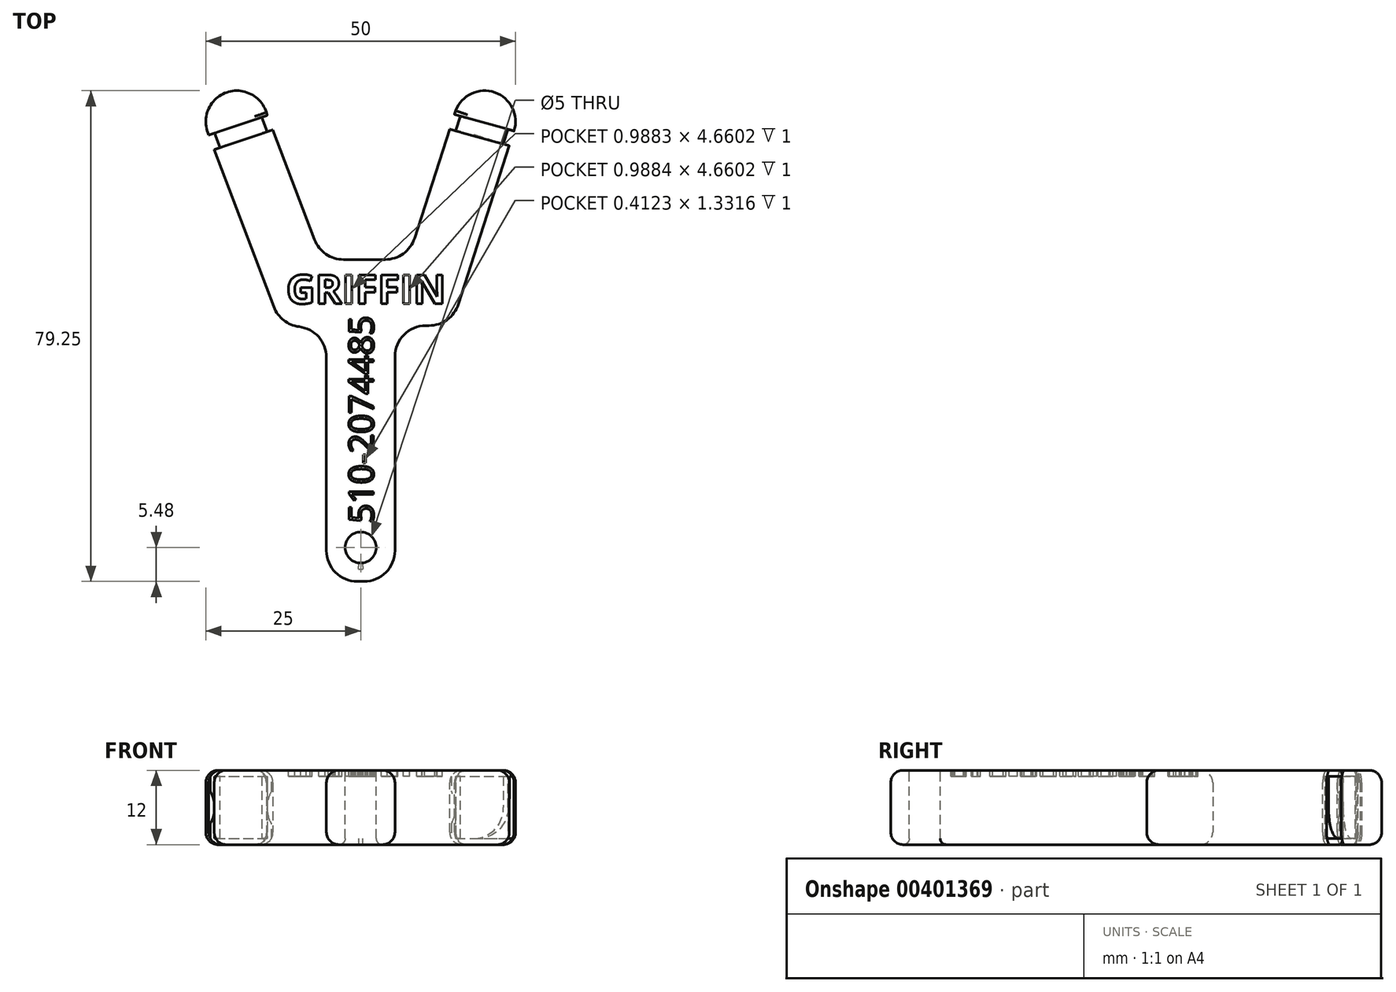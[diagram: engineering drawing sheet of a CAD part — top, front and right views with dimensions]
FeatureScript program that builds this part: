
annotation { "Feature Type Name" : "Feature", "Feature Type Description" : "" }
export const myFeature = defineFeature(function(context is Context, id is Id, definition is map)
    precondition{}
    {
        {
            var Q0;
            Q0=qCreatedBy(makeId("Top.planeOp"),FACE);
            var sketch = newSketch(context, id + "F0", { "sketchPlane" : qUnion([Q0])});
            skCircle(sketch, "E0", {"center": v(-20, 22.27) * mm, "radius": 1.5 * mm, "construction": true});
            skCircle(sketch, "E1", {"center": v(20, 22.27) * mm, "radius": 1.5 * mm, "construction": true});
            skArc(sketch, "E2", {"start": v(-15.23, 23.77) * mm, "mid": v(-21.63, 27) * mm, "end": v(-24.68, 20.5) * mm});
            skArc(sketch, "E3", {"start": v(24.76, 20.74) * mm, "mid": v(21.65, 27) * mm, "end": v(15.33, 24.05) * mm});
            skLineSegment(sketch, "E4", {"start": v(-15.44, 24.32) * mm, "end": v(-7.44, 3.23) * mm});
            skLineSegment(sketch, "E5", {"start": v(15.33, 24.05) * mm, "end": v(8.7, 3.47) * mm});
            skLineSegment(sketch, "E6", {"start": v(3.94, 0) * mm, "end": v(-2.77, 0) * mm});
            skLineSegment(sketch, "E7", {"start": v(-24.68, 20.5) * mm, "end": v(-12.8, -10.8) * mm});
            skLineSegment(sketch, "E8", {"start": v(-12.8, -10.8) * mm, "end": v(-10.53, -10.8) * mm});
            skLineSegment(sketch, "E9", {"start": v(-5.53, -15.8) * mm, "end": v(-5.53, -46.98) * mm});
            skLineSegment(sketch, "E10", {"start": v(-0.53, -51.98) * mm, "end": v(0.53, -51.98) * mm});
            skLineSegment(sketch, "E11", {"start": v(5.53, -46.98) * mm, "end": v(5.53, -15.66) * mm});
            skLineSegment(sketch, "E12", {"start": v(10.53, -10.66) * mm, "end": v(14.65, -10.66) * mm});
            skLineSegment(sketch, "E13", {"start": v(14.65, -10.66) * mm, "end": v(24.76, 20.74) * mm});
            skPoint(sketch, "E14.visualSharp", {"position": v(7.58, 0) * mm});
            skArc(sketch, "E14.filletArc", {"start": v(3.94, 0) * mm, "mid": v(6.89, 0.96) * mm, "end": v(8.7, 3.47) * mm});
            skPoint(sketch, "E15.visualSharp", {"position": v(-6.22, 0) * mm});
            skArc(sketch, "E15.filletArc", {"start": v(-7.44, 3.23) * mm, "mid": v(-5.6, 0.89) * mm, "end": v(-2.77, 0) * mm});
            skPoint(sketch, "E16.visualSharp", {"position": v(-5.53, -10.8) * mm});
            skArc(sketch, "E16.filletArc", {"start": v(-5.53, -15.8) * mm, "mid": v(-7, -12.27) * mm, "end": v(-10.53, -10.8) * mm});
            skPoint(sketch, "E17.visualSharp", {"position": v(5.53, -10.66) * mm});
            skArc(sketch, "E17.filletArc", {"start": v(10.53, -10.66) * mm, "mid": v(7, -12.13) * mm, "end": v(5.53, -15.66) * mm});
            skPoint(sketch, "E18.visualSharp", {"position": v(-5.53, -51.98) * mm});
            skArc(sketch, "E18.filletArc", {"start": v(-5.53, -46.98) * mm, "mid": v(-4.07, -50.52) * mm, "end": v(-0.53, -51.98) * mm});
            skPoint(sketch, "E19.visualSharp", {"position": v(5.53, -51.98) * mm});
            skArc(sketch, "E19.filletArc", {"start": v(0.53, -51.98) * mm, "mid": v(4.07, -50.52) * mm, "end": v(5.53, -46.98) * mm});
            skLineSegment(sketch, "E20", {"start": v(-20, 22.27) * mm, "end": v(20, 22.27) * mm, "construction": true});
            skSolve(sketch);
        }
        {
            var Q0;
            Q0 = qSketchRegion(id + "F0", true);
            extrude(context, id + "F1", {"entities" : qUnion([Q0]), "depth" : 12 * mm});
        }
        {
            var Q0;
            Q0=makeQuery(id+"F1.opExtrude","CAP_EDGE",EDGE,{"disambiguationData":[OSD([sQuery(id+"F0.wireOp",EDGE,"E11")])],"isStart":false});
            var Q1;
            Q1=makeQuery(id+"F1.opExtrude","CAP_EDGE",EDGE,{"disambiguationData":[OSD([sQuery(id+"F0.wireOp",EDGE,"E11")])],"isStart":true});
            var Q2;
            Q2=makeQuery(id+"F1.opExtrude","CAP_EDGE",EDGE,{"disambiguationData":[OSD([sQuery(id+"F0.wireOp",EDGE,"E5")])],"isStart":false});
            var Q3;
            Q3=makeQuery(id+"F1.opExtrude","CAP_EDGE",EDGE,{"disambiguationData":[OSD([sQuery(id+"F0.wireOp",EDGE,"E7")])],"isStart":false});
            var Q4;
            Q4=makeQuery(id+"F1.opExtrude","CAP_EDGE",EDGE,{"disambiguationData":[OSD([sQuery(id+"F0.wireOp",EDGE,"E13")])],"isStart":false});
            var Q5;
            Q5=makeQuery(id+"F1.opExtrude","CAP_EDGE",EDGE,{"disambiguationData":[OSD([sQuery(id+"F0.wireOp",EDGE,"E7")])],"isStart":true});
            var Q6;
            Q6=makeQuery(id+"F1.opExtrude","CAP_EDGE",EDGE,{"disambiguationData":[OSD([sQuery(id+"F0.wireOp",EDGE,"E5")])],"isStart":true});
            var Q7;
            Q7=makeQuery(id+"F1.opExtrude","CAP_EDGE",EDGE,{"disambiguationData":[OSD([sQuery(id+"F0.wireOp",EDGE,"E3")])],"isStart":true});
            fillet(context, id + "F2", {"entities" : qUnion([Q0, Q1, Q2, Q3, Q4, Q5, Q6, Q7]), "radius" : 2 * mm, "tangentPropagation" : true, "allowEdgeOverflow" : false});
        }
        {
            var Q0;
            Q0=makeQuery(id+"F1.opExtrude","SWEPT_EDGE",EDGE,{"disambiguationData":[OSD([sQuery(id+"F0.wireOp",EDGE,"E12"),sQuery(id+"F0.wireOp",EDGE,"E13")])]});
            var Q1;
            Q1=makeQuery(id+"F1.opExtrude","SWEPT_EDGE",EDGE,{"disambiguationData":[OSD([sQuery(id+"F0.wireOp",EDGE,"E7"),sQuery(id+"F0.wireOp",EDGE,"E8")])]});
            fillet(context, id + "F3", {"entities" : qUnion([Q0, Q1]), "radius" : 5 * mm, "tangentPropagation" : true, "allowEdgeOverflow" : false});
        }
        {
            var Q0;
            {var subQ0=sQuery(id+"F0.wireOp",EDGE,"E17.filletArc");var subQ1=sQuery(id+"F0.wireOp",EDGE,"E12");var subQ3=sQuery(id+"F0.wireOp",EDGE,"E11");var subQ4=sQuery(id+"F0.wireOp",EDGE,"E19.filletArc");var subQ5=sQuery(id+"F0.wireOp",EDGE,"E10");var subQ6=sQuery(id+"F0.wireOp",EDGE,"E18.filletArc");var subQ7=sQuery(id+"F0.wireOp",EDGE,"E9");var subQ8=sQuery(id+"F0.wireOp",EDGE,"E16.filletArc");var subQ9=sQuery(id+"F0.wireOp",EDGE,"E7");var subQ11=sQuery(id+"F0.wireOp",EDGE,"E13");var subQ13=sQuery(id+"F0.wireOp",EDGE,"E2");var subQ14=sQuery(id+"F0.wireOp",EDGE,"E3");var subQ15=sQuery(id+"F0.wireOp",EDGE,"E4");var subQ16=sQuery(id+"F0.wireOp",EDGE,"E5");var subQ17=sQuery(id+"F0.wireOp",EDGE,"E14.filletArc");var subQ18=sQuery(id+"F0.wireOp",EDGE,"E15.filletArc");var subQ19=sQuery(id+"F0.wireOp",EDGE,"E8");var subQ20=sQuery(id+"F0.wireOp",EDGE,"E6");Q0=makeQuery(id+"FMvpqk9PQKdqIEh_1.boolean.opBoolean","SPLIT",FACE,{"disambiguationData":[TD([makeQuery(id+"FMvpqk9PQKdqIEh_1.opExtrude","SWEPT_FACE",FACE,{"disambiguationData":[OSD([sQuery(id+"F1o8DMfexFJQnr1_1.wireOp",EDGE,"53e53609-d0ec-47c9-9e38-76e709d51a37.sketch_text.stroke-0")])]})])],"derivedFrom":makeQuery(id+"F1.opExtrude","CAP_FACE",FACE,{"disambiguationData":[OSD([subQ13,subQ14,subQ15,subQ16,subQ20,subQ9,subQ19,subQ7,subQ5,subQ3,subQ1,subQ11,subQ17,subQ18,subQ8,subQ0,subQ6,subQ4])],"isStart":false})});}
            var sketch = newSketch(context, id + "F4", { "sketchPlane" : qUnion([Q0])});
            skLineSegment(sketch, "E21", {"start": v(-27.54, 19.1) * mm, "end": v(-11.76, 24.4) * mm});
            skLineSegment(sketch, "E22", {"start": v(-26.64, 16.76) * mm, "end": v(-11.27, 21.93) * mm});
            skLineSegment(sketch, "E23", {"start": v(-11.76, 24.4) * mm, "end": v(-11.27, 21.93) * mm});
            skLineSegment(sketch, "E24", {"start": v(-27.54, 19.1) * mm, "end": v(-26.64, 16.76) * mm});
            skLineSegment(sketch, "E25", {"start": v(-22.8, 21.21) * mm, "end": v(-17.12, 23.12) * mm, "construction": true});
            skLineSegment(sketch, "E26", {"start": v(17.21, 23.38) * mm, "end": v(22.86, 21.35) * mm, "construction": true});
            skLineSegment(sketch, "E27", {"start": v(12.4, 24.2) * mm, "end": v(32, 18.77) * mm});
            skLineSegment(sketch, "E28", {"start": v(11.53, 21.84) * mm, "end": v(32, 16.18) * mm});
            skLineSegment(sketch, "E29", {"start": v(12.4, 24.2) * mm, "end": v(11.53, 21.84) * mm});
            skLineSegment(sketch, "E30", {"start": v(32, 18.77) * mm, "end": v(32, 16.18) * mm});
            skSolve(sketch);
        }
        {
            var Q0;
            Q0 = qSketchRegion(id + "F4", true);
            extrude(context, id + "F5", {"entities" : qUnion([Q0]), "operationType" : NewBodyOperationType.REMOVE, "oppositeDirection" : true, "depth" : 1 * mm});
        }
        {
            var Q0;
            Q0=makeQuery(id+"F1.opExtrude","CAP_FACE",FACE,{"disambiguationData":[OSD([sQuery(id+"F0.wireOp",EDGE,"E2"),sQuery(id+"F0.wireOp",EDGE,"E3"),sQuery(id+"F0.wireOp",EDGE,"E4"),sQuery(id+"F0.wireOp",EDGE,"E5"),sQuery(id+"F0.wireOp",EDGE,"E6"),sQuery(id+"F0.wireOp",EDGE,"E7"),sQuery(id+"F0.wireOp",EDGE,"E8"),sQuery(id+"F0.wireOp",EDGE,"E9"),sQuery(id+"F0.wireOp",EDGE,"E10"),sQuery(id+"F0.wireOp",EDGE,"E11"),sQuery(id+"F0.wireOp",EDGE,"E12"),sQuery(id+"F0.wireOp",EDGE,"E13"),sQuery(id+"F0.wireOp",EDGE,"E14.filletArc"),sQuery(id+"F0.wireOp",EDGE,"E15.filletArc"),sQuery(id+"F0.wireOp",EDGE,"E16.filletArc"),sQuery(id+"F0.wireOp",EDGE,"E17.filletArc"),sQuery(id+"F0.wireOp",EDGE,"E18.filletArc"),sQuery(id+"F0.wireOp",EDGE,"E19.filletArc")])],"isStart":true});
            var sketch = newSketch(context, id + "F6", { "sketchPlane" : qUnion([Q0])});
            skLineSegment(sketch, "E31.0", {"start": v(-27.54, -19.1) * mm, "end": v(-11.76, -24.4) * mm});
            skLineSegment(sketch, "E31.1", {"start": v(-26.64, -16.76) * mm, "end": v(-11.27, -21.93) * mm});
            skLineSegment(sketch, "E31.2", {"start": v(-11.76, -24.4) * mm, "end": v(-11.27, -21.93) * mm});
            skLineSegment(sketch, "E31.3", {"start": v(-27.54, -19.1) * mm, "end": v(-26.64, -16.76) * mm});
            skLineSegment(sketch, "E31.4", {"start": v(-22.8, -21.21) * mm, "end": v(-17.12, -23.12) * mm});
            skLineSegment(sketch, "E31.5", {"start": v(17.21, -23.38) * mm, "end": v(22.86, -21.35) * mm});
            skLineSegment(sketch, "E31.6", {"start": v(12.4, -24.2) * mm, "end": v(32, -18.77) * mm});
            skLineSegment(sketch, "E31.7", {"start": v(11.53, -21.84) * mm, "end": v(32, -16.18) * mm});
            skLineSegment(sketch, "E31.8", {"start": v(12.4, -24.2) * mm, "end": v(11.53, -21.84) * mm});
            skLineSegment(sketch, "E31.9", {"start": v(32, -18.77) * mm, "end": v(32, -16.18) * mm});
            skSolve(sketch);
        }
        {
            var Q0;
            Q0 = qSketchRegion(id + "F6", true);
            extrude(context, id + "F7", {"entities" : qUnion([Q0]), "operationType" : NewBodyOperationType.REMOVE, "oppositeDirection" : true, "depth" : 1 * mm});
        }
        {
            var Q0;
            Q0=makeQuery(id+"F1.opExtrude","SWEPT_FACE",FACE,{"disambiguationData":[OSD([sQuery(id+"F0.wireOp",EDGE,"E7")])]});
            var sketch = newSketch(context, id + "F8", { "sketchPlane" : qUnion([Q0])});
            skLineSegment(sketch, "E32.0", {"start": v(-27.48, 1) * mm, "end": v(-24.98, 1) * mm});
            skLineSegment(sketch, "E33.0", {"start": v(-24.98, 11) * mm, "end": v(-27.48, 11) * mm});
            skLineSegment(sketch, "E34", {"start": v(-27.48, 1) * mm, "end": v(-27.48, 11) * mm});
            skLineSegment(sketch, "E35", {"start": v(-24.98, 1) * mm, "end": v(-24.98, 11) * mm});
            skSolve(sketch);
        }
        {
            var Q0;
            Q0 = qSketchRegion(id + "F8", true);
            extrude(context, id + "F9", {"entities" : qUnion([Q0]), "operationType" : NewBodyOperationType.REMOVE, "oppositeDirection" : true, "depth" : 1 * mm});
        }
        {
            var Q0;
            Q0=makeQuery(id+"F1.opExtrude","SWEPT_FACE",FACE,{"disambiguationData":[OSD([sQuery(id+"F0.wireOp",EDGE,"E13")])]});
            var sketch = newSketch(context, id + "F10", { "sketchPlane" : qUnion([Q0])});
            skLineSegment(sketch, "E36.1", {"start": v(27.33, 11) * mm, "end": v(24.85, 11) * mm});
            skLineSegment(sketch, "E37.0", {"start": v(24.85, 1) * mm, "end": v(27.33, 1) * mm});
            skLineSegment(sketch, "E38", {"start": v(27.33, 11) * mm, "end": v(27.33, 1) * mm});
            skLineSegment(sketch, "E39", {"start": v(24.85, 11) * mm, "end": v(24.85, 1) * mm});
            skSolve(sketch);
        }
        {
            var Q0;
            Q0 = qSketchRegion(id + "F10", true);
            extrude(context, id + "F11", {"entities" : qUnion([Q0]), "operationType" : NewBodyOperationType.REMOVE, "oppositeDirection" : true, "depth" : 1 * mm});
        }
        {
            var Q0;
            Q0=makeQuery(id+"F1.opExtrude","SWEPT_FACE",FACE,{"disambiguationData":[OSD([sQuery(id+"F0.wireOp",EDGE,"E5")])]});
            var sketch = newSketch(context, id + "F12", { "sketchPlane" : qUnion([Q0])});
            skLineSegment(sketch, "E40.0", {"start": v(-26.96, 1) * mm, "end": v(-24.45, 1) * mm});
            skLineSegment(sketch, "E41.0", {"start": v(-24.45, 11) * mm, "end": v(-26.96, 11) * mm});
            skLineSegment(sketch, "E42", {"start": v(-26.96, 1) * mm, "end": v(-26.96, 11) * mm});
            skLineSegment(sketch, "E43", {"start": v(-24.45, 1) * mm, "end": v(-24.45, 11) * mm});
            skSolve(sketch);
        }
        {
            var Q0;
            Q0 = qSketchRegion(id + "F12", true);
            extrude(context, id + "F13", {"entities" : qUnion([Q0]), "operationType" : NewBodyOperationType.REMOVE, "oppositeDirection" : true, "depth" : 1 * mm});
        }
        {
            var Q0;
            Q0 = qSketchRegion(id + "F12", true);
            extrude(context, id + "F14", {"entities" : qUnion([Q0]), "operationType" : NewBodyOperationType.REMOVE, "oppositeDirection" : true, "depth" : 1 * mm});
        }
        {
            var Q0;
            Q0=makeQuery(id+"F1.opExtrude","SWEPT_FACE",FACE,{"disambiguationData":[OSD([sQuery(id+"F0.wireOp",EDGE,"E4")])]});
            var sketch = newSketch(context, id + "F15", { "sketchPlane" : qUnion([Q0])});
            skLineSegment(sketch, "E44.0", {"start": v(27.12, 11) * mm, "end": v(24.62, 11) * mm});
            skLineSegment(sketch, "E45.0", {"start": v(24.62, 1) * mm, "end": v(27.12, 1) * mm});
            skLineSegment(sketch, "E46", {"start": v(27.12, 11) * mm, "end": v(27.12, 1) * mm});
            skLineSegment(sketch, "E47", {"start": v(24.62, 11) * mm, "end": v(24.62, 1) * mm});
            skSolve(sketch);
        }
        {
            var Q0;
            Q0 = qSketchRegion(id + "F15", true);
            extrude(context, id + "F16", {"entities" : qUnion([Q0]), "operationType" : NewBodyOperationType.REMOVE, "oppositeDirection" : true, "depth" : 1 * mm});
        }
        {
            var Q0;
            {var subQ0=sQuery(id+"F15.wireOp",EDGE,"E45.0");Q0=makeQuery(id+"F16.boolean.opBoolean","COPY",EDGE,{"disambiguationData":[topologyDisambiguationEdgeConnected([makeQuery(id+"F7.boolean.opBoolean","COPY",FACE,{"derivedFrom":makeQuery(id+"F7.opExtrude","CAP_FACE",FACE,{"disambiguationData":[OSD([sQuery(id+"F6.wireOp",EDGE,"E31.0"),sQuery(id+"F6.wireOp",EDGE,"E31.1"),sQuery(id+"F6.wireOp",EDGE,"E31.2"),sQuery(id+"F6.wireOp",EDGE,"E31.3")])],"isStart":false})})])],"derivedFrom":makeQuery(id+"F16.opExtrude","CAP_EDGE",EDGE,{"disambiguationData":[OSD([subQ0])],"isStart":false})});}
            fillet(context, id + "F17", {"entities" : qUnion([Q0]), "radius" : 5 * mm, "tangentPropagation" : true, "allowEdgeOverflow" : false});
        }
        {
            var Q0;
            {var subQ0=sQuery(id+"F8.wireOp",EDGE,"E32.0");Q0=makeQuery(id+"F9.boolean.opBoolean","COPY",EDGE,{"disambiguationData":[topologyDisambiguationEdgeConnected([makeQuery(id+"F7.boolean.opBoolean","COPY",FACE,{"derivedFrom":makeQuery(id+"F7.opExtrude","CAP_FACE",FACE,{"disambiguationData":[OSD([sQuery(id+"F6.wireOp",EDGE,"E31.0"),sQuery(id+"F6.wireOp",EDGE,"E31.1"),sQuery(id+"F6.wireOp",EDGE,"E31.2"),sQuery(id+"F6.wireOp",EDGE,"E31.3")])],"isStart":false})})])],"derivedFrom":makeQuery(id+"F9.opExtrude","CAP_EDGE",EDGE,{"disambiguationData":[OSD([subQ0])],"isStart":false})});}
            fillet(context, id + "F18", {"entities" : qUnion([Q0]), "radius" : 5 * mm, "tangentPropagation" : true, "allowEdgeOverflow" : false});
        }
        {
            var Q0;
            {var subQ0=sQuery(id+"F8.wireOp",EDGE,"E33.0");Q0=makeQuery(id+"F9.boolean.opBoolean","COPY",EDGE,{"disambiguationData":[topologyDisambiguationEdgeConnected([makeQuery(id+"F5.boolean.opBoolean","COPY",FACE,{"derivedFrom":makeQuery(id+"F5.opExtrude","CAP_FACE",FACE,{"disambiguationData":[OSD([sQuery(id+"F4.wireOp",EDGE,"E21"),sQuery(id+"F4.wireOp",EDGE,"E22"),sQuery(id+"F4.wireOp",EDGE,"E23"),sQuery(id+"F4.wireOp",EDGE,"E24")])],"isStart":false})})])],"derivedFrom":makeQuery(id+"F9.opExtrude","CAP_EDGE",EDGE,{"disambiguationData":[OSD([subQ0])],"isStart":false})});}
            fillet(context, id + "F19", {"entities" : qUnion([Q0]), "radius" : 5 * mm, "tangentPropagation" : true, "allowEdgeOverflow" : false});
        }
        {
            var Q0;
            {var subQ0=sQuery(id+"F15.wireOp",EDGE,"E44.0");Q0=makeQuery(id+"F16.boolean.opBoolean","COPY",EDGE,{"disambiguationData":[topologyDisambiguationEdgeConnected([makeQuery(id+"F5.boolean.opBoolean","COPY",FACE,{"derivedFrom":makeQuery(id+"F5.opExtrude","CAP_FACE",FACE,{"disambiguationData":[OSD([sQuery(id+"F4.wireOp",EDGE,"E21"),sQuery(id+"F4.wireOp",EDGE,"E22"),sQuery(id+"F4.wireOp",EDGE,"E23"),sQuery(id+"F4.wireOp",EDGE,"E24")])],"isStart":false})})])],"derivedFrom":makeQuery(id+"F16.opExtrude","CAP_EDGE",EDGE,{"disambiguationData":[OSD([subQ0])],"isStart":false})});}
            fillet(context, id + "F20", {"entities" : qUnion([Q0]), "radius" : 5 * mm, "tangentPropagation" : true, "allowEdgeOverflow" : false});
        }
        {
            var Q0;
            {var subQ0=sQuery(id+"F12.wireOp",EDGE,"E40.0");Q0=makeQuery(id+"F13.boolean.opBoolean","COPY",EDGE,{"disambiguationData":[topologyDisambiguationEdgeConnected([makeQuery(id+"F7.boolean.opBoolean","COPY",FACE,{"derivedFrom":makeQuery(id+"F7.opExtrude","CAP_FACE",FACE,{"disambiguationData":[OSD([sQuery(id+"F6.wireOp",EDGE,"E31.6"),sQuery(id+"F6.wireOp",EDGE,"E31.7"),sQuery(id+"F6.wireOp",EDGE,"E31.8"),sQuery(id+"F6.wireOp",EDGE,"E31.9")])],"isStart":false})})])],"derivedFrom":makeQuery(id+"F13.opExtrude","CAP_EDGE",EDGE,{"disambiguationData":[OSD([subQ0])],"isStart":false})});}
            fillet(context, id + "F21", {"entities" : qUnion([Q0]), "radius" : 5 * mm, "tangentPropagation" : true, "allowEdgeOverflow" : false});
        }
        {
            var Q0;
            {var subQ0=sQuery(id+"F10.wireOp",EDGE,"E37.0");Q0=makeQuery(id+"F11.boolean.opBoolean","COPY",EDGE,{"disambiguationData":[topologyDisambiguationEdgeConnected([makeQuery(id+"F7.boolean.opBoolean","COPY",FACE,{"derivedFrom":makeQuery(id+"F7.opExtrude","CAP_FACE",FACE,{"disambiguationData":[OSD([sQuery(id+"F6.wireOp",EDGE,"E31.6"),sQuery(id+"F6.wireOp",EDGE,"E31.7"),sQuery(id+"F6.wireOp",EDGE,"E31.8"),sQuery(id+"F6.wireOp",EDGE,"E31.9")])],"isStart":false})})])],"derivedFrom":makeQuery(id+"F11.opExtrude","CAP_EDGE",EDGE,{"disambiguationData":[OSD([subQ0])],"isStart":false})});}
            fillet(context, id + "F22", {"entities" : qUnion([Q0]), "radius" : 5 * mm, "tangentPropagation" : true, "allowEdgeOverflow" : false});
        }
        {
            var Q0;
            {var subQ0=sQuery(id+"F10.wireOp",EDGE,"E36.1");Q0=makeQuery(id+"F11.boolean.opBoolean","COPY",EDGE,{"disambiguationData":[topologyDisambiguationEdgeConnected([makeQuery(id+"F5.boolean.opBoolean","COPY",FACE,{"derivedFrom":makeQuery(id+"F5.opExtrude","CAP_FACE",FACE,{"disambiguationData":[OSD([sQuery(id+"F4.wireOp",EDGE,"E27"),sQuery(id+"F4.wireOp",EDGE,"E28"),sQuery(id+"F4.wireOp",EDGE,"E29"),sQuery(id+"F4.wireOp",EDGE,"E30")])],"isStart":false})})])],"derivedFrom":makeQuery(id+"F11.opExtrude","CAP_EDGE",EDGE,{"disambiguationData":[OSD([subQ0])],"isStart":false})});}
            fillet(context, id + "F23", {"entities" : qUnion([Q0]), "radius" : 5 * mm, "tangentPropagation" : true, "allowEdgeOverflow" : false});
        }
        {
            var Q0;
            {var subQ0=sQuery(id+"F12.wireOp",EDGE,"E41.0");Q0=makeQuery(id+"F13.boolean.opBoolean","COPY",EDGE,{"disambiguationData":[topologyDisambiguationEdgeConnected([makeQuery(id+"F5.boolean.opBoolean","COPY",FACE,{"derivedFrom":makeQuery(id+"F5.opExtrude","CAP_FACE",FACE,{"disambiguationData":[OSD([sQuery(id+"F4.wireOp",EDGE,"E27"),sQuery(id+"F4.wireOp",EDGE,"E28"),sQuery(id+"F4.wireOp",EDGE,"E29"),sQuery(id+"F4.wireOp",EDGE,"E30")])],"isStart":false})})])],"derivedFrom":makeQuery(id+"F13.opExtrude","CAP_EDGE",EDGE,{"disambiguationData":[OSD([subQ0])],"isStart":false})});}
            fillet(context, id + "F24", {"entities" : qUnion([Q0]), "radius" : 5 * mm, "tangentPropagation" : true, "allowEdgeOverflow" : false});
        }
        {
            var Q0;
            {var subQ0=sQuery(id+"F0.wireOp",EDGE,"E14.filletArc");var subQ1=sQuery(id+"F0.wireOp",EDGE,"E13");var subQ3=sQuery(id+"F0.wireOp",EDGE,"E12");var subQ5=sQuery(id+"F0.wireOp",EDGE,"E11");var subQ6=sQuery(id+"F0.wireOp",EDGE,"E10");var subQ7=sQuery(id+"F0.wireOp",EDGE,"E9");var subQ8=sQuery(id+"F0.wireOp",EDGE,"E4");var subQ9=sQuery(id+"F0.wireOp",EDGE,"E5");var subQ10=sQuery(id+"F0.wireOp",EDGE,"E6");var subQ11=sQuery(id+"F0.wireOp",EDGE,"E7");var subQ13=sQuery(id+"F0.wireOp",EDGE,"E15.filletArc");var subQ14=sQuery(id+"F0.wireOp",EDGE,"E16.filletArc");var subQ15=sQuery(id+"F0.wireOp",EDGE,"E17.filletArc");var subQ16=sQuery(id+"F0.wireOp",EDGE,"E18.filletArc");var subQ17=sQuery(id+"F0.wireOp",EDGE,"E19.filletArc");var subQ18=sQuery(id+"F0.wireOp",EDGE,"E8");Q0=makeQuery(id+"F5.boolean.opBoolean","SPLIT",FACE,{"disambiguationData":[TD([makeQuery(id+"F5.opExtrude","SWEPT_FACE",FACE,{"disambiguationData":[OSD([sQuery(id+"F4.wireOp",EDGE,"E22")])]})])],"derivedFrom":makeQuery(id+"F1.opExtrude","CAP_FACE",FACE,{"disambiguationData":[OSD([sQuery(id+"F0.wireOp",EDGE,"E2"),sQuery(id+"F0.wireOp",EDGE,"E3"),subQ8,subQ9,subQ10,subQ11,subQ18,subQ7,subQ6,subQ5,subQ3,subQ1,subQ0,subQ13,subQ14,subQ15,subQ16,subQ17])],"isStart":false})});}
            var sketch = newSketch(context, id + "F25", { "sketchPlane" : qUnion([Q0])});
            skText(sketch, "E48", { "text": "GRIFFIN", "fontName": "OpenSans-Bold.ttf"});
            const initialGuessF25  = {"E48": [-0.01205, -0.00713, 1, 0, 0.0047]};
            skSetInitialGuess(sketch, initialGuessF25);
            skSolve(sketch);
        }
        {
            var Q0;
            Q0 = qSketchRegion(id + "F25", true);
            extrude(context, id + "F26", {"entities" : qUnion([Q0]), "operationType" : NewBodyOperationType.REMOVE, "oppositeDirection" : true, "depth" : 1 * mm});
        }
        {
            var Q0;
            {var subQ0=sQuery(id+"F0.wireOp",EDGE,"E14.filletArc");var subQ2=sQuery(id+"F0.wireOp",EDGE,"E13");var subQ5=sQuery(id+"F0.wireOp",EDGE,"E12");var subQ8=sQuery(id+"F0.wireOp",EDGE,"E11");var subQ10=sQuery(id+"F0.wireOp",EDGE,"E10");var subQ12=sQuery(id+"F0.wireOp",EDGE,"E9");var subQ14=sQuery(id+"F0.wireOp",EDGE,"E4");var subQ16=sQuery(id+"F0.wireOp",EDGE,"E5");var subQ18=sQuery(id+"F0.wireOp",EDGE,"E6");var subQ20=sQuery(id+"F0.wireOp",EDGE,"E8");var subQ21=sQuery(id+"F0.wireOp",EDGE,"E7");var subQ26=sQuery(id+"F0.wireOp",EDGE,"E15.filletArc");var subQ29=sQuery(id+"F0.wireOp",EDGE,"E19.filletArc");var subQ31=sQuery(id+"F0.wireOp",EDGE,"E16.filletArc");var subQ33=sQuery(id+"F0.wireOp",EDGE,"E17.filletArc");var subQ35=sQuery(id+"F0.wireOp",EDGE,"E18.filletArc");var subQ37=makeQuery(id+"F5.opExtrude","SWEPT_FACE",FACE,{"disambiguationData":[OSD([sQuery(id+"F4.wireOp",EDGE,"E22")])]});Q0=makeQuery(id+"F26.boolean.opBoolean","SPLIT",FACE,{"disambiguationData":[TD([makeQuery(id+"F5.boolean.opBoolean","COPY",FACE,{"derivedFrom":subQ37})])],"derivedFrom":makeQuery(id+"F5.boolean.opBoolean","SPLIT",FACE,{"disambiguationData":[TD([subQ37])],"derivedFrom":makeQuery(id+"F1.opExtrude","CAP_FACE",FACE,{"disambiguationData":[OSD([sQuery(id+"F0.wireOp",EDGE,"E2"),sQuery(id+"F0.wireOp",EDGE,"E3"),subQ14,subQ16,subQ18,subQ21,subQ20,subQ12,subQ10,subQ8,subQ5,subQ2,subQ0,subQ26,subQ31,subQ33,subQ35,subQ29])],"isStart":false})})});}
            var sketch = newSketch(context, id + "F27", { "sketchPlane" : qUnion([Q0])});
            skText(sketch, "E49", { "text": "510-2074485", "fontName": "OpenSans-Regular.ttf"});
            const initialGuessF27  = {"E49": [0.00208, -0.04262, 0, 1, 0.004]};
            skSetInitialGuess(sketch, initialGuessF27);
            skSolve(sketch);
        }
        {
            var Q0;
            Q0 = qSketchRegion(id + "F27", true);
            extrude(context, id + "F28", {"entities" : qUnion([Q0]), "operationType" : NewBodyOperationType.REMOVE, "oppositeDirection" : true, "depth" : 1 * mm});
        }
        {
            var Q0;
            {var subQ2=sQuery(id+"F0.wireOp",EDGE,"E13");var subQ7=sQuery(id+"F0.wireOp",EDGE,"E12");var subQ11=sQuery(id+"F0.wireOp",EDGE,"E10");var subQ14=sQuery(id+"F0.wireOp",EDGE,"E5");var subQ17=sQuery(id+"F0.wireOp",EDGE,"E4");var subQ43=sQuery(id+"F0.wireOp",EDGE,"E8");var subQ44=sQuery(id+"F0.wireOp",EDGE,"E7");var subQ48=sQuery(id+"F0.wireOp",EDGE,"E14.filletArc");var subQ53=sQuery(id+"F0.wireOp",EDGE,"E15.filletArc");var subQ59=sQuery(id+"F0.wireOp",EDGE,"E19.filletArc");var subQ65=sQuery(id+"F0.wireOp",EDGE,"E17.filletArc");var subQ70=sQuery(id+"F0.wireOp",EDGE,"E18.filletArc");var subQ73=makeQuery(id+"F5.opExtrude","SWEPT_FACE",FACE,{"disambiguationData":[OSD([sQuery(id+"F4.wireOp",EDGE,"E22")])]});var subQ74=makeQuery(id+"F5.boolean.opBoolean","COPY",FACE,{"derivedFrom":subQ73});var subQ81=sQuery(id+"F0.wireOp",EDGE,"E6");var subQ90=sQuery(id+"F0.wireOp",EDGE,"E9");var subQ95=sQuery(id+"F0.wireOp",EDGE,"E11");var subQ102=sQuery(id+"F0.wireOp",EDGE,"E16.filletArc");Q0=makeQuery(id+"F28.boolean.opBoolean","SPLIT",FACE,{"disambiguationData":[TD([subQ74])],"derivedFrom":makeQuery(id+"F26.boolean.opBoolean","SPLIT",FACE,{"disambiguationData":[TD([subQ74])],"derivedFrom":makeQuery(id+"F5.boolean.opBoolean","SPLIT",FACE,{"disambiguationData":[TD([subQ73])],"derivedFrom":makeQuery(id+"F1.opExtrude","CAP_FACE",FACE,{"disambiguationData":[OSD([sQuery(id+"F0.wireOp",EDGE,"E2"),sQuery(id+"F0.wireOp",EDGE,"E3"),subQ17,subQ14,subQ81,subQ44,subQ43,subQ90,subQ11,subQ95,subQ7,subQ2,subQ48,subQ53,subQ102,subQ65,subQ70,subQ59])],"isStart":false})})})});}
            var sketch = newSketch(context, id + "F29", { "sketchPlane" : qUnion([Q0])});
            skCircle(sketch, "E50", {"center": v(0, -46.5) * mm, "radius": 2.5 * mm});
            skSolve(sketch);
        }
        {
            var Q0;
            Q0 = qSketchRegion(id + "F29", true);
            extrude(context, id + "F30", {"entities" : qUnion([Q0]), "operationType" : NewBodyOperationType.REMOVE, "oppositeDirection" : true, "depth" : 25 * mm});
        }
        {
            var Q0;
            Q0=makeQuery(id+"F30.boolean.opBoolean","COPY",EDGE,{"derivedFrom":makeQuery(id+"F30.opExtrude","CAP_EDGE",EDGE,{"disambiguationData":[OSD([sQuery(id+"F29.wireOp",EDGE,"E50")])],"isStart":true})});
            var Q1;
            {var subQ0=sQuery(id+"F0.wireOp",EDGE,"E14.filletArc");var subQ1=sQuery(id+"F0.wireOp",EDGE,"E13");var subQ3=sQuery(id+"F0.wireOp",EDGE,"E12");var subQ5=sQuery(id+"F0.wireOp",EDGE,"E11");var subQ6=sQuery(id+"F0.wireOp",EDGE,"E10");var subQ7=sQuery(id+"F0.wireOp",EDGE,"E9");var subQ8=sQuery(id+"F0.wireOp",EDGE,"E4");var subQ9=sQuery(id+"F0.wireOp",EDGE,"E5");var subQ10=sQuery(id+"F0.wireOp",EDGE,"E6");var subQ11=sQuery(id+"F0.wireOp",EDGE,"E7");var subQ13=sQuery(id+"F0.wireOp",EDGE,"E15.filletArc");var subQ14=sQuery(id+"F0.wireOp",EDGE,"E16.filletArc");var subQ15=sQuery(id+"F0.wireOp",EDGE,"E17.filletArc");var subQ16=sQuery(id+"F0.wireOp",EDGE,"E18.filletArc");var subQ17=sQuery(id+"F0.wireOp",EDGE,"E19.filletArc");var subQ18=sQuery(id+"F0.wireOp",EDGE,"E8");Q1=makeQuery(id+"F30.boolean.opBoolean","INTERSECT",EDGE,{"derivedFrom":[makeQuery(id+"F7.boolean.opBoolean","SPLIT",FACE,{"disambiguationData":[TD([makeQuery(id+"F7.opExtrude","SWEPT_FACE",FACE,{"disambiguationData":[OSD([sQuery(id+"F6.wireOp",EDGE,"E31.1")])]})])],"derivedFrom":makeQuery(id+"F1.opExtrude","CAP_FACE",FACE,{"disambiguationData":[OSD([sQuery(id+"F0.wireOp",EDGE,"E2"),sQuery(id+"F0.wireOp",EDGE,"E3"),subQ8,subQ9,subQ10,subQ11,subQ18,subQ7,subQ6,subQ5,subQ3,subQ1,subQ0,subQ13,subQ14,subQ15,subQ16,subQ17])],"isStart":true})}),makeQuery(id+"F30.opExtrude","SWEPT_FACE",FACE,{"disambiguationData":[OSD([sQuery(id+"F29.wireOp",EDGE,"E50")])]})]});}
            fillet(context, id + "F31", {"entities" : qUnion([Q0, Q1]), "radius" : 1 * mm, "tangentPropagation" : true, "allowEdgeOverflow" : false});
        }
    });
